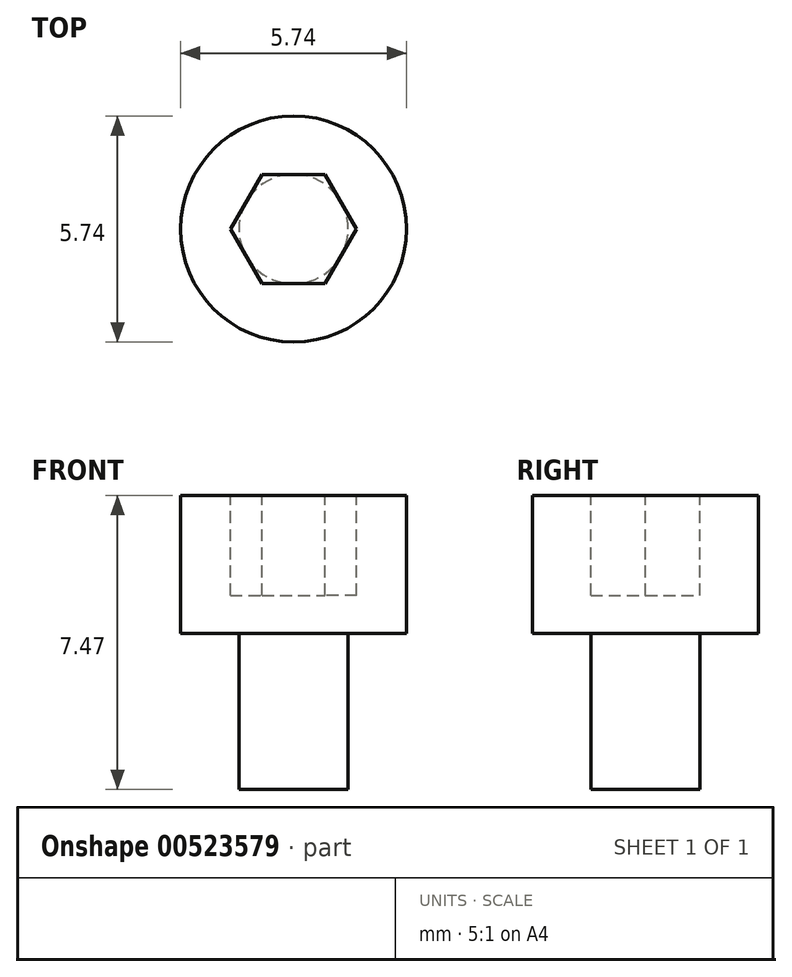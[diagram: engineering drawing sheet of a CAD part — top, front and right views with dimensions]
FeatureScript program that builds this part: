
annotation { "Feature Type Name" : "Feature", "Feature Type Description" : "" }
export const myFeature = defineFeature(function(context is Context, id is Id, definition is map)
    precondition{}
    {
        {
            var Q0;
            Q0=qCreatedBy(makeId("Front.planeOp"),FACE);
            var sketch = newSketch(context, id + "F0", { "sketchPlane" : qUnion([Q0])});
            skLineSegment(sketch, "E0", {"start": v(0, 0) * mm, "end": v(-2.87, 0) * mm});
            skLineSegment(sketch, "E1", {"start": v(-2.87, 0) * mm, "end": v(-2.87, -3.5) * mm});
            skLineSegment(sketch, "E2", {"start": v(-1.39, -3.5) * mm, "end": v(-1.39, -7.47) * mm});
            skLineSegment(sketch, "E3", {"start": v(-1.39, -7.47) * mm, "end": v(0, -7.47) * mm});
            skLineSegment(sketch, "E4", {"start": v(-1.39, -3.5) * mm, "end": v(-2.87, -3.5) * mm});
            skLineSegment(sketch, "E5", {"start": v(0, 0) * mm, "end": v(0, -7.47) * mm});
            skSolve(sketch);
        }
        {
            var Q0;
            Q0=makeQuery(id+"F0.imprint","IMPRINT",FACE,{"disambiguationData":[TD([[makeQuery(id+"F0.imprint","IMPRINT",EDGE,{"derivedFrom":sQuery(id+"F0.wireOp",EDGE,"E0")}),1.0]])]});
            var Q1;
            Q1=sQuery(id+"F0.wireOp",EDGE,"E5");
            revolve(context, id + "F1", {"entities" : qUnion([Q0]), "axis" : qUnion([Q1]), "revolveType" : RevolveType.FULL});
        }
        {
            var Q0;
            Q0=makeQuery(id+"F1.opRevolve","SWEPT_FACE",FACE,{"disambiguationData":[OSD([sQuery(id+"F0.wireOp",EDGE,"E0")])]});
            var sketch = newSketch(context, id + "F2", { "sketchPlane" : qUnion([Q0])});
            skCircle(sketch, "E6.cCircle", {"center": v(0, 0) * mm, "radius": 1.39 * mm, "construction": true});
            skLineSegment(sketch, "E6.0", {"start": v(-0.8, 1.39) * mm, "end": v(0.8, 1.39) * mm});
            skLineSegment(sketch, "E6.1", {"start": v(0.8, 1.39) * mm, "end": v(1.6, 0) * mm});
            skLineSegment(sketch, "E6.2", {"start": v(1.6, 0) * mm, "end": v(0.8, -1.39) * mm});
            skLineSegment(sketch, "E6.3", {"start": v(0.8, -1.39) * mm, "end": v(-0.8, -1.39) * mm});
            skLineSegment(sketch, "E6.4", {"start": v(-0.8, -1.39) * mm, "end": v(-1.6, 0) * mm});
            skLineSegment(sketch, "E6.5", {"start": v(-1.6, 0) * mm, "end": v(-0.8, 1.39) * mm});
            skPoint(sketch, "E6.0.midPoint", {"position": v(0, 1.39) * mm});
            skSolve(sketch);
        }
        {
            var Q0;
            Q0=makeQuery(id+"F2.imprint","IMPRINT",FACE,{"disambiguationData":[TD([[makeQuery(id+"F2.imprint","IMPRINT",EDGE,{"derivedFrom":sQuery(id+"F2.wireOp",EDGE,"E6.0")}),-1.0]])]});
            extrude(context, id + "F3", {"entities" : qUnion([Q0]), "operationType" : NewBodyOperationType.REMOVE, "oppositeDirection" : true, "depth" : 2.54 * mm, "offsetDistance" : 25.4 * mm});
        }
    });
